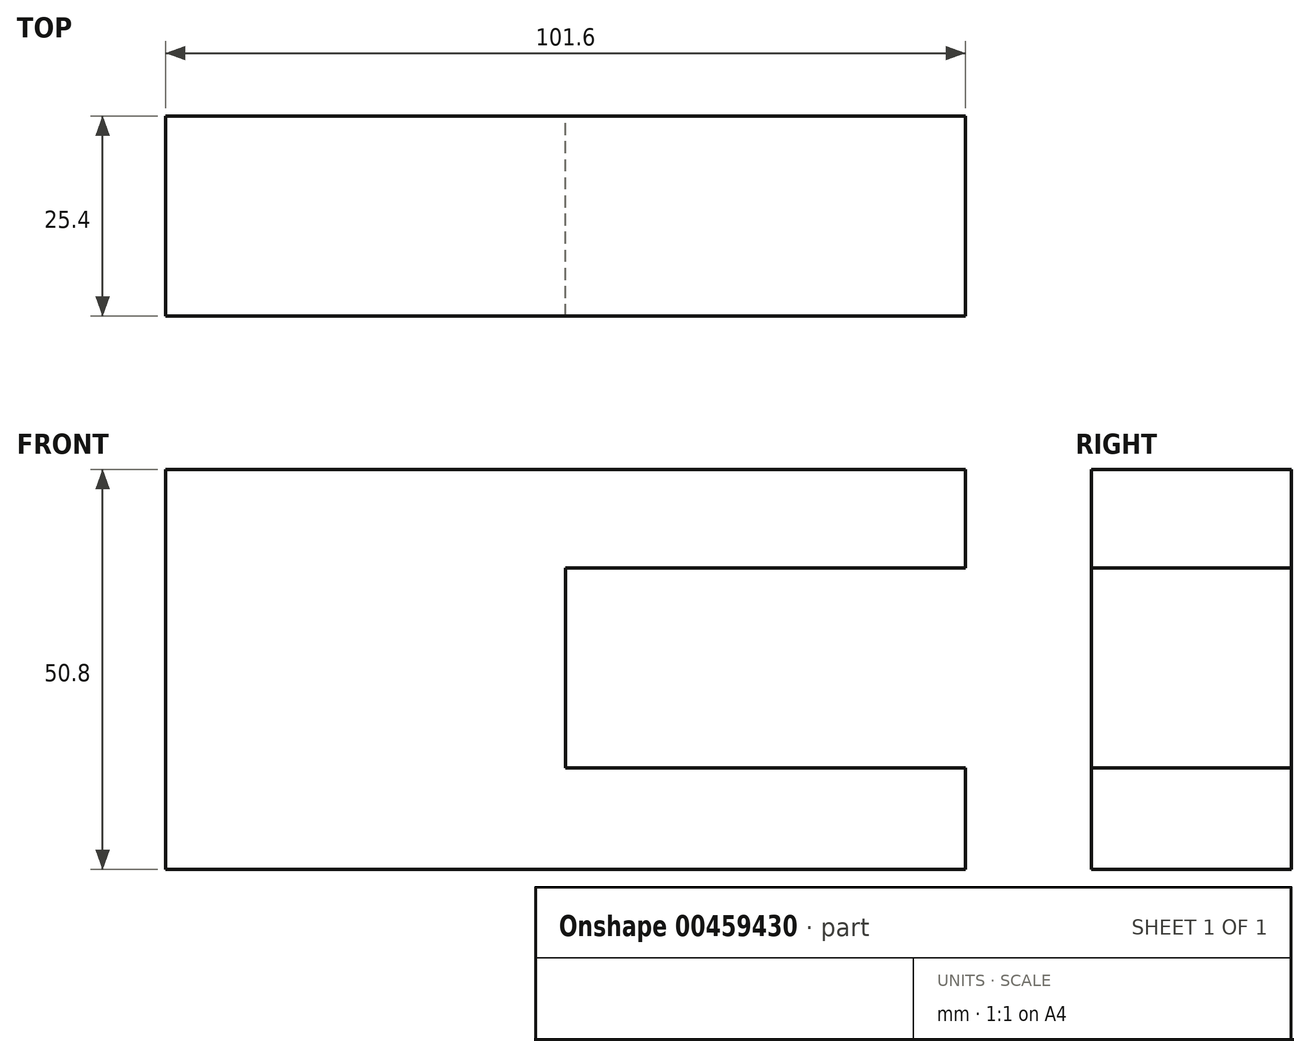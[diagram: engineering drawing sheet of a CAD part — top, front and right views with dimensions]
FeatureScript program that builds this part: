
annotation { "Feature Type Name" : "Feature", "Feature Type Description" : "" }
export const myFeature = defineFeature(function(context is Context, id is Id, definition is map)
    precondition{}
    {
        {
            var Q0;
            Q0=qCreatedBy(makeId("Front.planeOp"),FACE);
            var sketch = newSketch(context, id + "F0", { "sketchPlane" : qUnion([Q0])});
            skLineSegment(sketch, "E0.bottom", {"start": v(50.8, -25.4) * mm, "end": v(-50.8, -25.4) * mm});
            skLineSegment(sketch, "E0.top", {"start": v(50.8, 25.4) * mm, "end": v(-50.8, 25.4) * mm});
            skLineSegment(sketch, "E0.left", {"start": v(50.8, -25.4) * mm, "end": v(50.8, 25.4) * mm});
            skLineSegment(sketch, "E0.right", {"start": v(-50.8, -25.4) * mm, "end": v(-50.8, 25.4) * mm});
            skPoint(sketch, "E0.middle", {"position": v(0, 0) * mm});
            skSolve(sketch);
        }
        {
            var Q0;
            Q0=makeQuery(id+"F0.imprint","IMPRINT",FACE,{"disambiguationData":[TD([[makeQuery(id+"F0.imprint","IMPRINT",EDGE,{"derivedFrom":sQuery(id+"F0.wireOp",EDGE,"E0.bottom")}),-1.0]])]});
            extrude(context, id + "F1", {"entities" : qUnion([Q0]), "depth" : 25.4 * mm});
        }
        {
            var Q0;
            Q0=qCreatedBy(makeId("Front.planeOp"),FACE);
            var sketch = newSketch(context, id + "F2", { "sketchPlane" : qUnion([Q0])});
            skLineSegment(sketch, "E1.bottom", {"start": v(50.8, 12.87) * mm, "end": v(0, 12.87) * mm});
            skLineSegment(sketch, "E1.top", {"start": v(50.8, -12.53) * mm, "end": v(0, -12.53) * mm});
            skLineSegment(sketch, "E1.left", {"start": v(50.8, 12.87) * mm, "end": v(50.8, -12.53) * mm});
            skLineSegment(sketch, "E1.right", {"start": v(0, 12.87) * mm, "end": v(0, -12.53) * mm});
            skSolve(sketch);
        }
        {
            var Q0;
            Q0=makeQuery(id+"F2.imprint","IMPRINT",FACE,{"disambiguationData":[TD([[makeQuery(id+"F2.imprint","IMPRINT",EDGE,{"derivedFrom":sQuery(id+"F2.wireOp",EDGE,"E1.bottom")}),1.0]])]});
            extrude(context, id + "F3", {"entities" : qUnion([Q0]), "operationType" : NewBodyOperationType.REMOVE, "endBound" : BoundingType.THROUGH_ALL, "depth" : 25.4 * mm});
        }
    });
